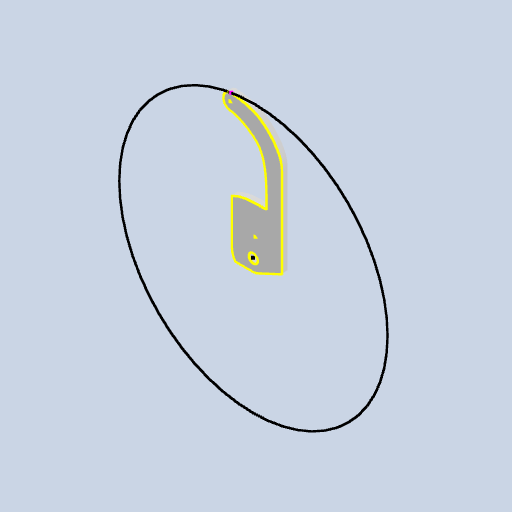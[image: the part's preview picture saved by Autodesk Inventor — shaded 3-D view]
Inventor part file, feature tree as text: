
AUTODESK INVENTOR PART (.ipt)
format: ipt  version: 2022 (Build 260153000, 153)  size: 195,072 bytes
history: native  units: mm
features: other x5, reference x3, sketch x2, extrude x1, projected_geometry x1
ambient origin geometry x8: Origin, YZ Plane, XZ Plane, XY Plane, X Axis, Y Axis, Z Axis, Center Point
bodies: Body1 (feature_tree)
feature tree (12):
  other  "Твердое тело1"
  extrude  "Выдавливание1"  Depth=7.6mm
  sketch  "Эскиз2"
  sketch  "Эскиз1"
  reference  "Ссылка1"
  reference  "Ссылка2"
  reference  "Ссылка3"
  projected_geometry  "Спроецированная петля1"
  other  "<userpath>\Documents\Git\MZCAT_2024\MZCAT_2.iam"
  other  "MZCAT_2.iam"
  other  "CAT_protector:1"
  other  "base:1"
